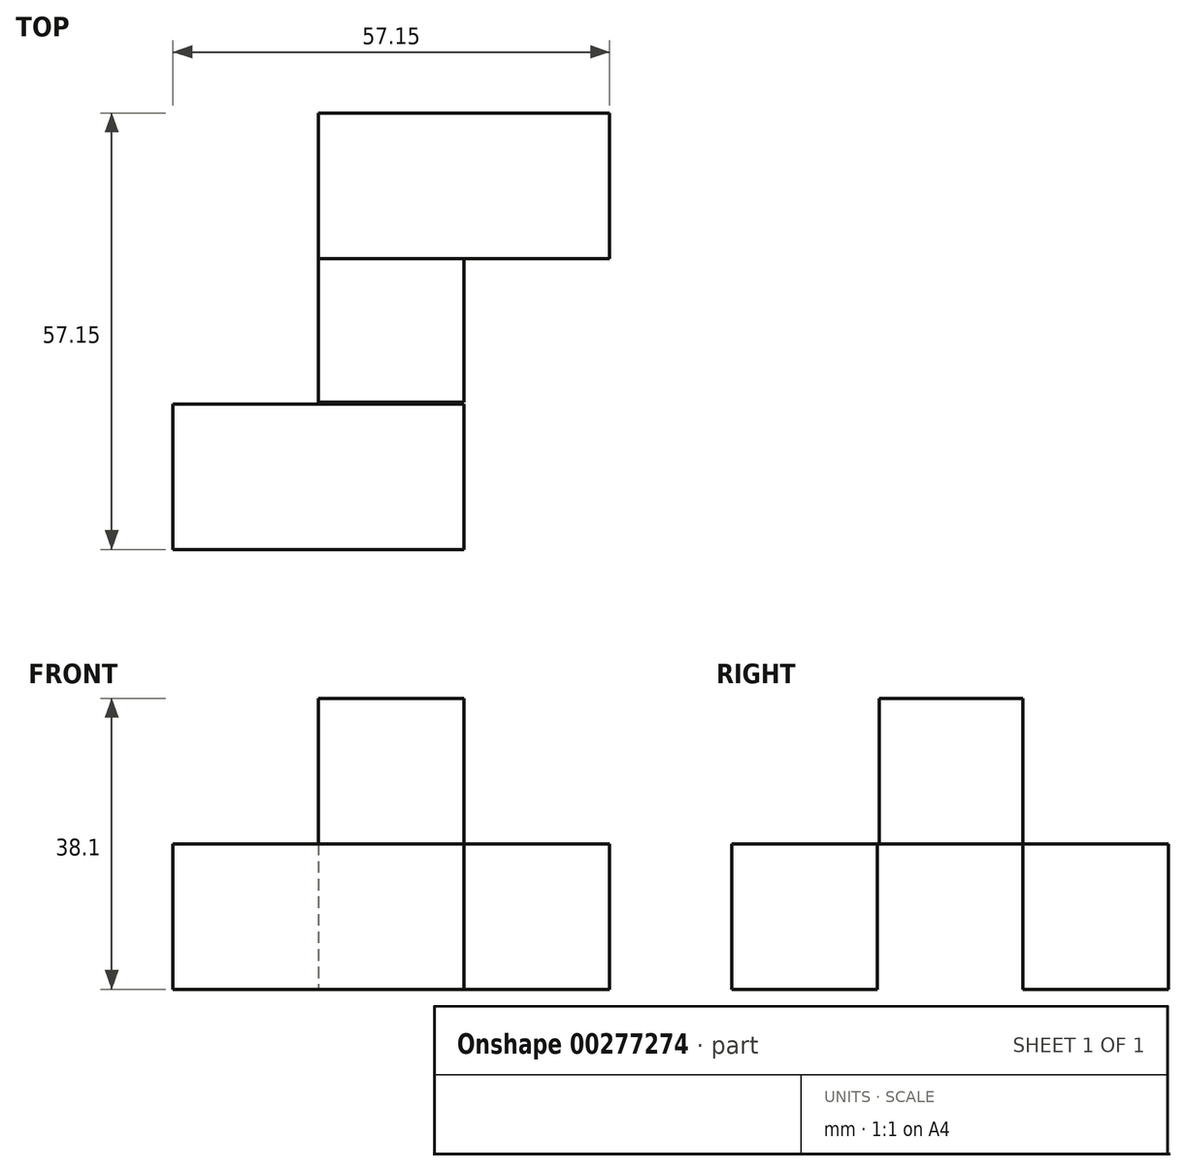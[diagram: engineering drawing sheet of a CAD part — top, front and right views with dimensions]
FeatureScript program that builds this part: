
annotation { "Feature Type Name" : "Feature", "Feature Type Description" : "" }
export const myFeature = defineFeature(function(context is Context, id is Id, definition is map)
    precondition{}
    {
        {
            var Q0;
            Q0=qCreatedBy(makeId("Top.planeOp"),FACE);
            var sketch = newSketch(context, id + "F0", { "sketchPlane" : qUnion([Q0])});
            skLineSegment(sketch, "E0.bottom", {"start": v(24.53, 57.15) * mm, "end": v(43.58, 57.15) * mm});
            skLineSegment(sketch, "E0.top", {"start": v(24.53, 38.1) * mm, "end": v(43.58, 38.1) * mm});
            skLineSegment(sketch, "E0.left", {"start": v(24.53, 57.15) * mm, "end": v(24.53, 38.1) * mm});
            skLineSegment(sketch, "E0.right", {"start": v(43.58, 57.15) * mm, "end": v(43.58, 38.1) * mm});
            skLineSegment(sketch, "E1.bottom", {"start": v(24.53, 38.1) * mm, "end": v(5.48, 38.1) * mm});
            skLineSegment(sketch, "E1.top", {"start": v(24.53, 57.15) * mm, "end": v(5.48, 57.15) * mm});
            skLineSegment(sketch, "E1.left", {"start": v(24.53, 38.1) * mm, "end": v(24.53, 57.15) * mm});
            skLineSegment(sketch, "E1.right", {"start": v(5.48, 38.1) * mm, "end": v(5.48, 57.15) * mm});
            skLineSegment(sketch, "E2.bottom", {"start": v(5.48, 38.1) * mm, "end": v(24.53, 38.1) * mm});
            skLineSegment(sketch, "E2.top", {"start": v(5.48, 19.05) * mm, "end": v(24.53, 19.05) * mm});
            skLineSegment(sketch, "E2.left", {"start": v(5.48, 38.1) * mm, "end": v(5.48, 19.05) * mm});
            skLineSegment(sketch, "E2.right", {"start": v(24.53, 38.1) * mm, "end": v(24.53, 19.05) * mm});
            skLineSegment(sketch, "E3.top", {"start": v(5.48, 0) * mm, "end": v(24.53, 0) * mm});
            skLineSegment(sketch, "E3.left", {"start": v(5.48, 19.05) * mm, "end": v(5.48, 0) * mm});
            skLineSegment(sketch, "E3.right", {"start": v(24.53, 19.05) * mm, "end": v(24.53, 0) * mm});
            skLineSegment(sketch, "E4.bottom", {"start": v(5.48, 19.05) * mm, "end": v(-13.57, 19.05) * mm});
            skLineSegment(sketch, "E4.top", {"start": v(5.48, 0) * mm, "end": v(-13.57, 0) * mm});
            skLineSegment(sketch, "E4.right", {"start": v(-13.57, 19.05) * mm, "end": v(-13.57, 0) * mm});
            skSolve(sketch);
        }
        {
            var Q0;
            Q0=makeQuery(id+"F0.imprint","IMPRINT",FACE,{"disambiguationData":[TD([[makeQuery(id+"F0.imprint","IMPRINT",EDGE,{"derivedFrom":sQuery(id+"F0.wireOp",EDGE,"E0.bottom")}),-1.0]])]});
            var Q1;
            Q1=makeQuery(id+"F0.imprint","IMPRINT",FACE,{"disambiguationData":[TD([[makeQuery(id+"F0.imprint","IMPRINT",EDGE,{"derivedFrom":sQuery(id+"F0.wireOp",EDGE,"E1.top")}),1.0]])]});
            var Q2;
            Q2=makeQuery(id+"F0.imprint","IMPRINT",FACE,{"disambiguationData":[TD([[makeQuery(id+"F0.imprint","IMPRINT",EDGE,{"derivedFrom":sQuery(id+"F0.wireOp",EDGE,"E2.top")}),-1.0]])]});
            var Q3;
            Q3=makeQuery(id+"F0.imprint","IMPRINT",FACE,{"disambiguationData":[TD([[makeQuery(id+"F0.imprint","IMPRINT",EDGE,{"derivedFrom":sQuery(id+"F0.wireOp",EDGE,"E4.bottom")}),1.0]])]});
            var Q4;
            Q4=makeQuery(id+"F0.imprint","IMPRINT",FACE,{"disambiguationData":[TD([[makeQuery(id+"F0.imprint","IMPRINT",EDGE,{"derivedFrom":sQuery(id+"F0.wireOp",EDGE,"E2.bottom")}),-1.0]])]});
            extrude(context, id + "F1", {"entities" : qUnion([Q0, Q1, Q2, Q3, Q4]), "depth" : 19.05 * mm});
        }
        {
            var Q0;
            Q0=makeQuery(id+"F1.opExtrude","CAP_FACE",FACE,{"disambiguationData":[OSD([sQuery(id+"F0.wireOp",EDGE,"E0.bottom"),sQuery(id+"F0.wireOp",EDGE,"E0.top"),sQuery(id+"F0.wireOp",EDGE,"E0.right"),sQuery(id+"F0.wireOp",EDGE,"E1.top"),sQuery(id+"F0.wireOp",EDGE,"E1.right"),sQuery(id+"F0.wireOp",EDGE,"E2.left"),sQuery(id+"F0.wireOp",EDGE,"E2.right"),sQuery(id+"F0.wireOp",EDGE,"E3.top"),sQuery(id+"F0.wireOp",EDGE,"E3.right"),sQuery(id+"F0.wireOp",EDGE,"E4.bottom"),sQuery(id+"F0.wireOp",EDGE,"E4.top"),sQuery(id+"F0.wireOp",EDGE,"E4.right")])],"isStart":false});
            var sketch = newSketch(context, id + "F2", { "sketchPlane" : qUnion([Q0])});
            skLineSegment(sketch, "E5.bottom", {"start": v(5.48, 38.1) * mm, "end": v(24.53, 38.1) * mm});
            skLineSegment(sketch, "E5.top", {"start": v(5.48, 19.3) * mm, "end": v(24.53, 19.3) * mm});
            skLineSegment(sketch, "E5.left", {"start": v(5.48, 38.1) * mm, "end": v(5.48, 19.3) * mm});
            skLineSegment(sketch, "E5.right", {"start": v(24.53, 38.1) * mm, "end": v(24.53, 19.3) * mm});
            skSolve(sketch);
        }
        {
            var Q0;
            Q0=makeQuery(id+"F2.imprint","IMPRINT",FACE,{"disambiguationData":[TD([[makeQuery(id+"F2.imprint","IMPRINT",EDGE,{"derivedFrom":sQuery(id+"F2.wireOp",EDGE,"E5.bottom")}),-1.0]])]});
            extrude(context, id + "F3", {"entities" : qUnion([Q0]), "operationType" : NewBodyOperationType.ADD, "depth" : 19.05 * mm});
        }
    });
